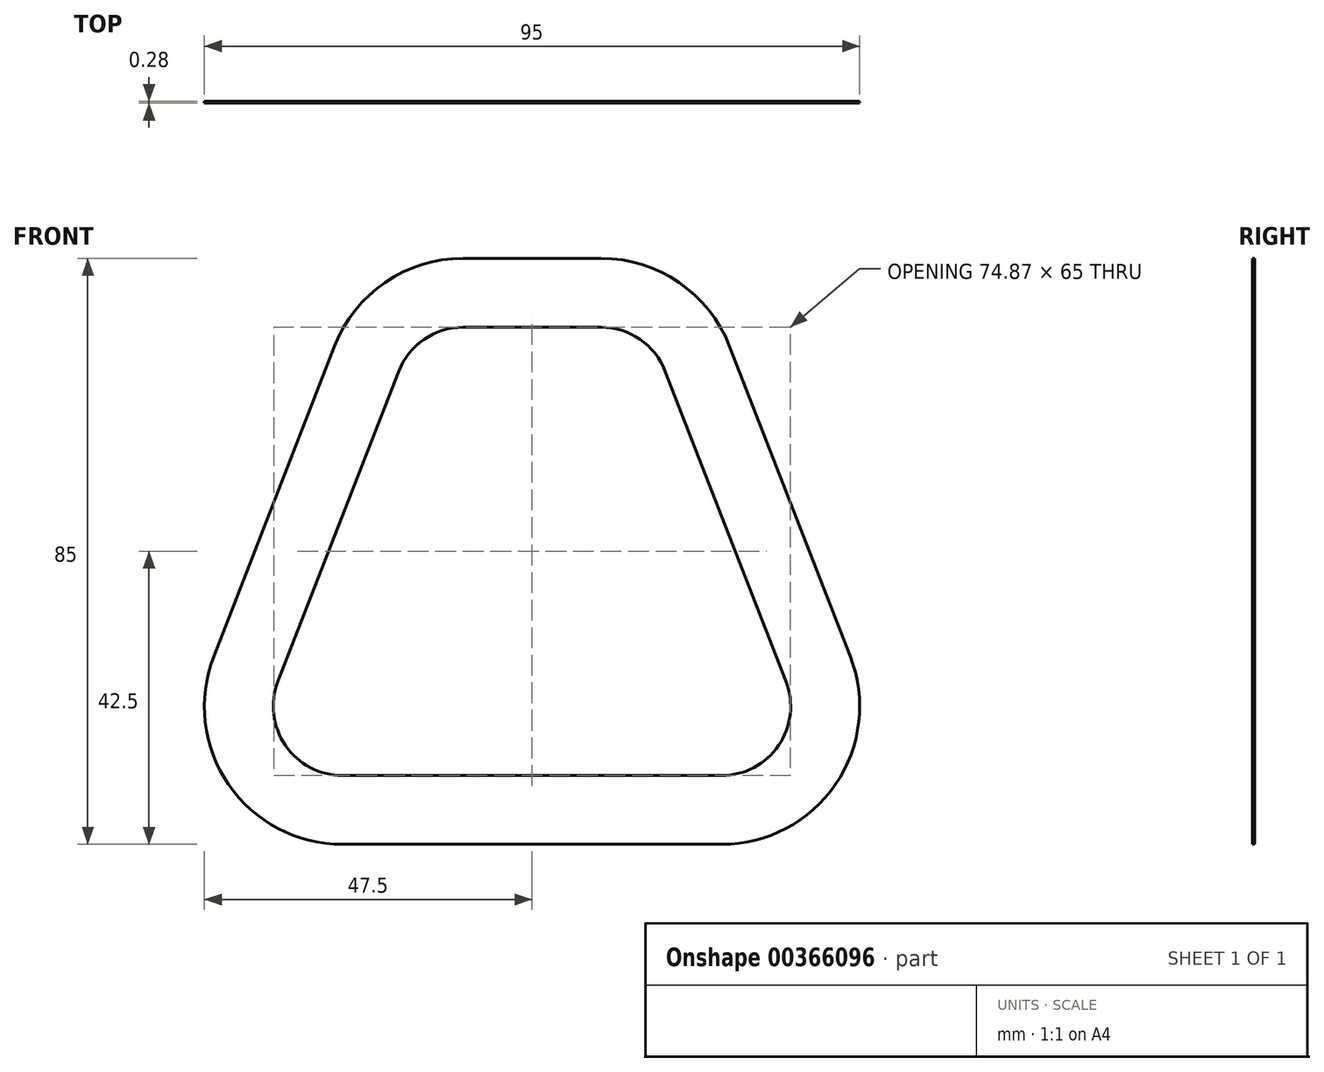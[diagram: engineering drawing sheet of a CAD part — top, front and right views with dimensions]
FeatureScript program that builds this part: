
annotation { "Feature Type Name" : "Feature", "Feature Type Description" : "" }
export const myFeature = defineFeature(function(context is Context, id is Id, definition is map)
    precondition{}
    {
        {
            var Q0;
            Q0=qCreatedBy(makeId("Front.planeOp"),FACE);
            var sketch = newSketch(context, id + "F0", { "sketchPlane" : qUnion([Q0])});
            skLineSegment(sketch, "E0", {"start": v(0, 0) * mm, "end": v(0, 20) * mm, "construction": true});
            skLineSegment(sketch, "E1", {"start": v(0, 20) * mm, "end": v(10, 20) * mm});
            skLineSegment(sketch, "E2", {"start": v(10, 20) * mm, "end": v(27.5, -25) * mm});
            skLineSegment(sketch, "E3", {"start": v(27.5, -25) * mm, "end": v(6.93, -25) * mm});
            skLineSegment(sketch, "E4", {"start": v(6.93, -25) * mm, "end": v(0, -13) * mm});
            skLineSegment(sketch, "E5", {"start": v(27.5, -25) * mm, "end": v(27.5, 20) * mm, "construction": true});
            skLineSegment(sketch, "E6", {"start": v(6.93, -25) * mm, "end": v(6.93, -13) * mm, "construction": true});
            skPoint(sketch, "E7.visualSharp", {"position": v(10, 20) * mm});
            skPoint(sketch, "E8.visualSharp", {"position": v(27.5, -25) * mm});
            skLineSegment(sketch, "E9.MirrorCS", {"start": v(0, 20) * mm, "end": v(-10, 20) * mm});
            skPoint(sketch, "E10.MirrorP", {"position": v(-27.5, -25) * mm});
            skLineSegment(sketch, "E11.MirrorCS", {"start": v(-10, 20) * mm, "end": v(-27.5, -25) * mm});
            skLineSegment(sketch, "E12.MirrorCS", {"start": v(-27.5, -25) * mm, "end": v(-6.93, -25) * mm});
            skLineSegment(sketch, "E13.MirrorCS", {"start": v(-27.5, -25) * mm, "end": v(-27.5, 20) * mm, "construction": true});
            skLineSegment(sketch, "E14.MirrorCS", {"start": v(-6.93, -25) * mm, "end": v(0, -13) * mm});
            skLineSegment(sketch, "E15.MirrorCS", {"start": v(-6.93, -25) * mm, "end": v(-6.93, -13) * mm, "construction": true});
            skLineSegment(sketch, "E16.0", {"start": v(0, 30) * mm, "end": v(10, 30) * mm});
            skLineSegment(sketch, "E16.1", {"start": v(0, 30) * mm, "end": v(-10, 30) * mm});
            skLineSegment(sketch, "E16.2", {"start": v(19.32, 23.62) * mm, "end": v(36.82, -21.38) * mm});
            skLineSegment(sketch, "E16.3", {"start": v(-19.32, 23.62) * mm, "end": v(-36.82, -21.38) * mm});
            skLineSegment(sketch, "E16.7", {"start": v(-27.5, -35) * mm, "end": v(27.5, -35) * mm});
            skLineSegment(sketch, "E17.0", {"start": v(-27.5, -45) * mm, "end": v(27.5, -45) * mm});
            skLineSegment(sketch, "E17.1", {"start": v(-28.64, 27.25) * mm, "end": v(-46.14, -17.75) * mm});
            skLineSegment(sketch, "E17.2", {"start": v(28.64, 27.25) * mm, "end": v(46.14, -17.75) * mm});
            skLineSegment(sketch, "E17.3", {"start": v(0, 40) * mm, "end": v(10, 40) * mm});
            skLineSegment(sketch, "E17.4", {"start": v(0, 40) * mm, "end": v(-10, 40) * mm});
            skPoint(sketch, "E18.visualSharp", {"position": v(-23.68, 40) * mm});
            skArc(sketch, "E18.filletArc", {"start": v(-10, 40) * mm, "mid": v(-21.3, 36.5) * mm, "end": v(-28.64, 27.25) * mm});
            skPoint(sketch, "E19.visualSharp", {"position": v(23.68, 40) * mm});
            skArc(sketch, "E19.filletArc", {"start": v(28.64, 27.25) * mm, "mid": v(21.3, 36.5) * mm, "end": v(10, 40) * mm});
            skPoint(sketch, "E20.visualSharp", {"position": v(56.74, -45) * mm});
            skArc(sketch, "E20.filletArc", {"start": v(27.5, -45) * mm, "mid": v(44, -36.3) * mm, "end": v(46.14, -17.75) * mm});
            skPoint(sketch, "E21.visualSharp", {"position": v(-56.74, -45) * mm});
            skArc(sketch, "E21.filletArc", {"start": v(-46.14, -17.75) * mm, "mid": v(-44, -36.3) * mm, "end": v(-27.5, -45) * mm});
            skPoint(sketch, "E22.visualSharp", {"position": v(-42.12, -35) * mm});
            skArc(sketch, "E22.filletArc", {"start": v(-36.82, -21.38) * mm, "mid": v(-35.75, -30.65) * mm, "end": v(-27.5, -35) * mm});
            skPoint(sketch, "E23.visualSharp", {"position": v(42.12, -35) * mm});
            skArc(sketch, "E23.filletArc", {"start": v(27.5, -35) * mm, "mid": v(35.75, -30.65) * mm, "end": v(36.82, -21.38) * mm});
            skPoint(sketch, "E24.visualSharp", {"position": v(16.84, 30) * mm});
            skArc(sketch, "E24.filletArc", {"start": v(19.32, 23.62) * mm, "mid": v(15.65, 28.25) * mm, "end": v(10, 30) * mm});
            skPoint(sketch, "E25.visualSharp", {"position": v(-16.84, 30) * mm});
            skArc(sketch, "E25.filletArc", {"start": v(-10, 30) * mm, "mid": v(-15.65, 28.25) * mm, "end": v(-19.32, 23.62) * mm});
            skSolve(sketch);
        }
        {
            var Q0;
            Q0 = qSketchRegion(id + "F0", true);
            extrude(context, id + "F1", {"entities" : qUnion([Q0]), "depth" : (0.45 / 1.6) * mm});
        }
    });
